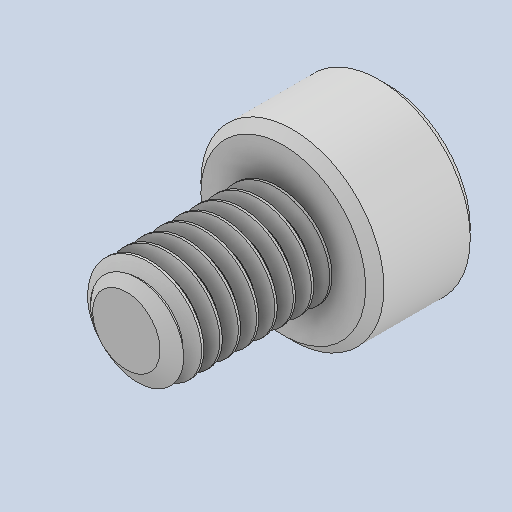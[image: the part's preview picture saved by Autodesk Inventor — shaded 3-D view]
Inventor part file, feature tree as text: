
AUTODESK INVENTOR PART (.ipt)
format: ipt  version: 2023 (Build 270158000, 158)  size: 392,192 bytes
history: native  units: in
note: dims shown in document units (in); Inventor stores cm internally (conversion verified against a paired STEP export)
features: chamfer x1
ambient origin geometry x8: Origin, YZ Plane, XZ Plane, XY Plane, X Axis, Y Axis, Z Axis, Center Point
bodies: Solid1 (feature_tree)
feature tree (1):
  chamfer  "Chamfer1"  [1 undecoded]
note: 1 required parameter value undecoded (feature->parameter linkage not recoverable at this tier; creation-order binding heuristic only, values carry confidence <= 0.55)
